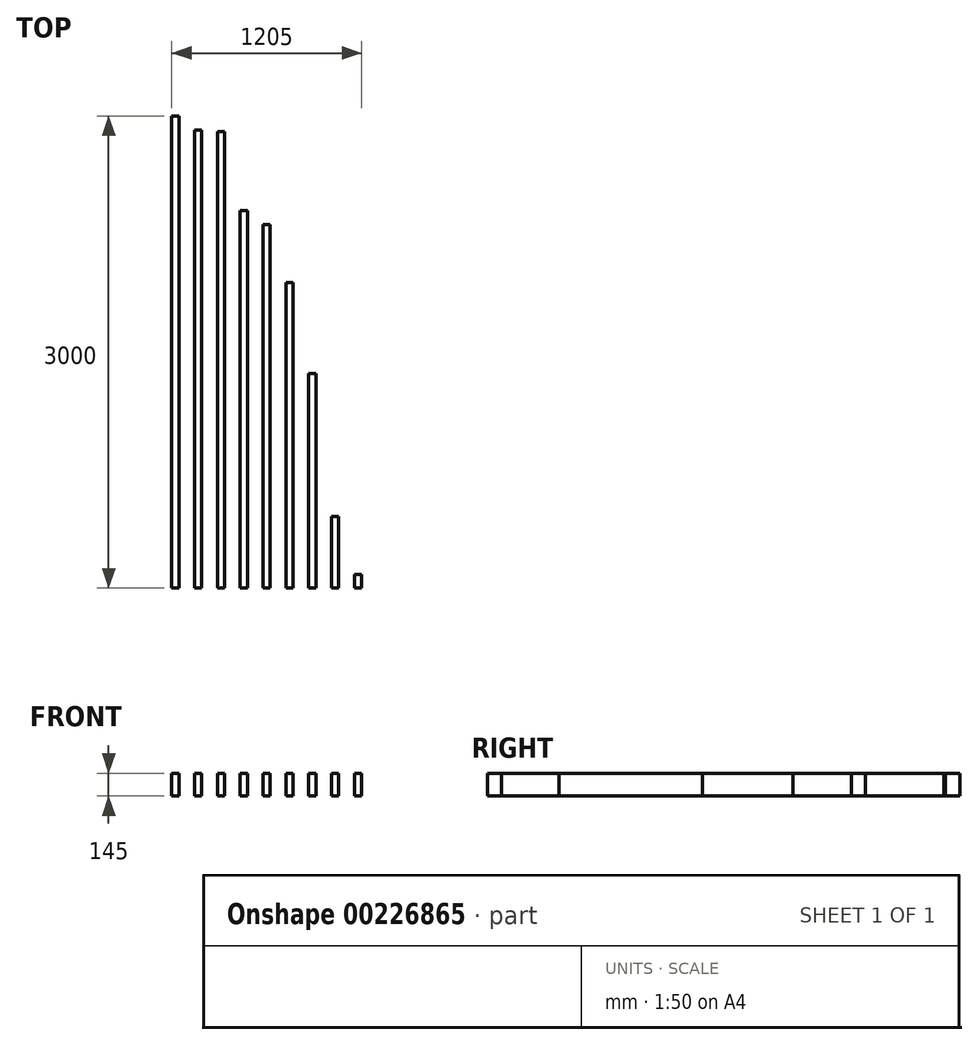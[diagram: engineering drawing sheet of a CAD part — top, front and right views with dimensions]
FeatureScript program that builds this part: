
annotation { "Feature Type Name" : "Feature", "Feature Type Description" : "" }
export const myFeature = defineFeature(function(context is Context, id is Id, definition is map)
    precondition{}
    {
        {
            var Q0;
            Q0=qCreatedBy(makeId("Front.planeOp"),FACE);
            var sketch = newSketch(context, id + "F0", { "sketchPlane" : qUnion([Q0])});
            skLineSegment(sketch, "E0.bottom", {"start": v(0, 0) * mm, "end": v(45, 0) * mm});
            skLineSegment(sketch, "E0.top", {"start": v(0, 145) * mm, "end": v(45, 145) * mm});
            skLineSegment(sketch, "E0.left", {"start": v(0, 0) * mm, "end": v(0, 145) * mm});
            skLineSegment(sketch, "E0.right", {"start": v(45, 0) * mm, "end": v(45, 145) * mm});
            skLineSegment(sketch, "E1.bottom", {"start": v(145, 0) * mm, "end": v(190, 0) * mm});
            skLineSegment(sketch, "E1.top", {"start": v(145, 145) * mm, "end": v(190, 145) * mm});
            skLineSegment(sketch, "E1.left", {"start": v(145, 0) * mm, "end": v(145, 145) * mm});
            skLineSegment(sketch, "E1.right", {"start": v(190, 0) * mm, "end": v(190, 145) * mm});
            skLineSegment(sketch, "E2.bottom", {"start": v(290, 0) * mm, "end": v(335, 0) * mm});
            skLineSegment(sketch, "E2.top", {"start": v(290, 145) * mm, "end": v(335, 145) * mm});
            skLineSegment(sketch, "E2.left", {"start": v(290, 0) * mm, "end": v(290, 145) * mm});
            skLineSegment(sketch, "E2.right", {"start": v(335, 0) * mm, "end": v(335, 145) * mm});
            skLineSegment(sketch, "E3.bottom", {"start": v(435, 0) * mm, "end": v(480, 0) * mm});
            skLineSegment(sketch, "E3.top", {"start": v(435, 145) * mm, "end": v(480, 145) * mm});
            skLineSegment(sketch, "E3.left", {"start": v(435, 0) * mm, "end": v(435, 145) * mm});
            skLineSegment(sketch, "E3.right", {"start": v(480, 0) * mm, "end": v(480, 145) * mm});
            skLineSegment(sketch, "E4.bottom", {"start": v(580, 0) * mm, "end": v(625, 0) * mm});
            skLineSegment(sketch, "E4.top", {"start": v(580, 145) * mm, "end": v(625, 145) * mm});
            skLineSegment(sketch, "E4.left", {"start": v(580, 0) * mm, "end": v(580, 145) * mm});
            skLineSegment(sketch, "E4.right", {"start": v(625, 0) * mm, "end": v(625, 145) * mm});
            skLineSegment(sketch, "E5.bottom", {"start": v(870, 0) * mm, "end": v(915, 0) * mm});
            skLineSegment(sketch, "E5.top", {"start": v(870, 145) * mm, "end": v(915, 145) * mm});
            skLineSegment(sketch, "E5.left", {"start": v(870, 0) * mm, "end": v(870, 145) * mm});
            skLineSegment(sketch, "E5.right", {"start": v(915, 0) * mm, "end": v(915, 145) * mm});
            skLineSegment(sketch, "E6.bottom", {"start": v(1015, 0) * mm, "end": v(1060, 0) * mm});
            skLineSegment(sketch, "E6.top", {"start": v(1015, 145) * mm, "end": v(1060, 145) * mm});
            skLineSegment(sketch, "E6.left", {"start": v(1015, 0) * mm, "end": v(1015, 145) * mm});
            skLineSegment(sketch, "E6.right", {"start": v(1060, 0) * mm, "end": v(1060, 145) * mm});
            skLineSegment(sketch, "E7.bottom", {"start": v(1160, 0) * mm, "end": v(1205, 0) * mm});
            skLineSegment(sketch, "E7.top", {"start": v(1160, 145) * mm, "end": v(1205, 145) * mm});
            skLineSegment(sketch, "E7.left", {"start": v(1160, 0) * mm, "end": v(1160, 145) * mm});
            skLineSegment(sketch, "E7.right", {"start": v(1205, 0) * mm, "end": v(1205, 145) * mm});
            skLineSegment(sketch, "E8.bottom", {"start": v(725, 0) * mm, "end": v(770, 0) * mm});
            skLineSegment(sketch, "E8.top", {"start": v(725, 145) * mm, "end": v(770, 145) * mm});
            skLineSegment(sketch, "E8.left", {"start": v(725, 0) * mm, "end": v(725, 145) * mm});
            skLineSegment(sketch, "E8.right", {"start": v(770, 0) * mm, "end": v(770, 145) * mm});
            skSolve(sketch);
        }
        {
            var Q0;
            Q0=makeQuery(id+"F0.imprint","IMPRINT",FACE,{"disambiguationData":[TD([[makeQuery(id+"F0.imprint","IMPRINT",EDGE,{"derivedFrom":sQuery(id+"F0.wireOp",EDGE,"E0.bottom")}),1.0]])]});
            extrude(context, id + "F1", {"entities" : qUnion([Q0]), "oppositeDirection" : true, "depth" : 3000 * mm});
        }
        {
            var Q0;
            Q0=makeQuery(id+"F0.imprint","IMPRINT",FACE,{"disambiguationData":[TD([[makeQuery(id+"F0.imprint","IMPRINT",EDGE,{"derivedFrom":sQuery(id+"F0.wireOp",EDGE,"E1.bottom")}),1.0]])]});
            extrude(context, id + "F2", {"entities" : qUnion([Q0]), "oppositeDirection" : true, "depth" : 2910 * mm});
        }
        {
            var Q0;
            Q0=makeQuery(id+"F0.imprint","IMPRINT",FACE,{"disambiguationData":[TD([[makeQuery(id+"F0.imprint","IMPRINT",EDGE,{"derivedFrom":sQuery(id+"F0.wireOp",EDGE,"E2.bottom")}),1.0]])]});
            extrude(context, id + "F3", {"entities" : qUnion([Q0]), "oppositeDirection" : true, "depth" : 2900 * mm});
        }
        {
            var Q0;
            Q0=makeQuery(id+"F0.imprint","IMPRINT",FACE,{"disambiguationData":[TD([[makeQuery(id+"F0.imprint","IMPRINT",EDGE,{"derivedFrom":sQuery(id+"F0.wireOp",EDGE,"E3.bottom")}),1.0]])]});
            extrude(context, id + "F4", {"entities" : qUnion([Q0]), "oppositeDirection" : true, "depth" : 2400 * mm});
        }
        {
            var Q0;
            Q0=makeQuery(id+"F0.imprint","IMPRINT",FACE,{"disambiguationData":[TD([[makeQuery(id+"F0.imprint","IMPRINT",EDGE,{"derivedFrom":sQuery(id+"F0.wireOp",EDGE,"E4.bottom")}),1.0]])]});
            extrude(context, id + "F5", {"entities" : qUnion([Q0]), "oppositeDirection" : true, "depth" : 2310 * mm});
        }
        {
            var Q0;
            Q0=makeQuery(id+"F0.imprint","IMPRINT",FACE,{"disambiguationData":[TD([[makeQuery(id+"F0.imprint","IMPRINT",EDGE,{"derivedFrom":sQuery(id+"F0.wireOp",EDGE,"E5.bottom")}),1.0]])]});
            extrude(context, id + "F6", {"entities" : qUnion([Q0]), "oppositeDirection" : true, "depth" : 1365 * mm});
        }
        {
            var Q0;
            Q0=makeQuery(id+"F0.imprint","IMPRINT",FACE,{"disambiguationData":[TD([[makeQuery(id+"F0.imprint","IMPRINT",EDGE,{"derivedFrom":sQuery(id+"F0.wireOp",EDGE,"E6.bottom")}),1.0]])]});
            extrude(context, id + "F7", {"entities" : qUnion([Q0]), "oppositeDirection" : true, "depth" : 455 * mm});
        }
        {
            var Q0;
            Q0=makeQuery(id+"F0.imprint","IMPRINT",FACE,{"disambiguationData":[TD([[makeQuery(id+"F0.imprint","IMPRINT",EDGE,{"derivedFrom":sQuery(id+"F0.wireOp",EDGE,"E7.bottom")}),1.0]])]});
            extrude(context, id + "F8", {"entities" : qUnion([Q0]), "oppositeDirection" : true, "depth" : 87.5 * mm});
        }
        {
            var Q0;
            Q0=makeQuery(id+"F0.imprint","IMPRINT",FACE,{"disambiguationData":[TD([[makeQuery(id+"F0.imprint","IMPRINT",EDGE,{"derivedFrom":sQuery(id+"F0.wireOp",EDGE,"E8.bottom")}),1.0]])]});
            extrude(context, id + "F9", {"entities" : qUnion([Q0]), "oppositeDirection" : true, "depth" : 1940 * mm});
        }
    });
